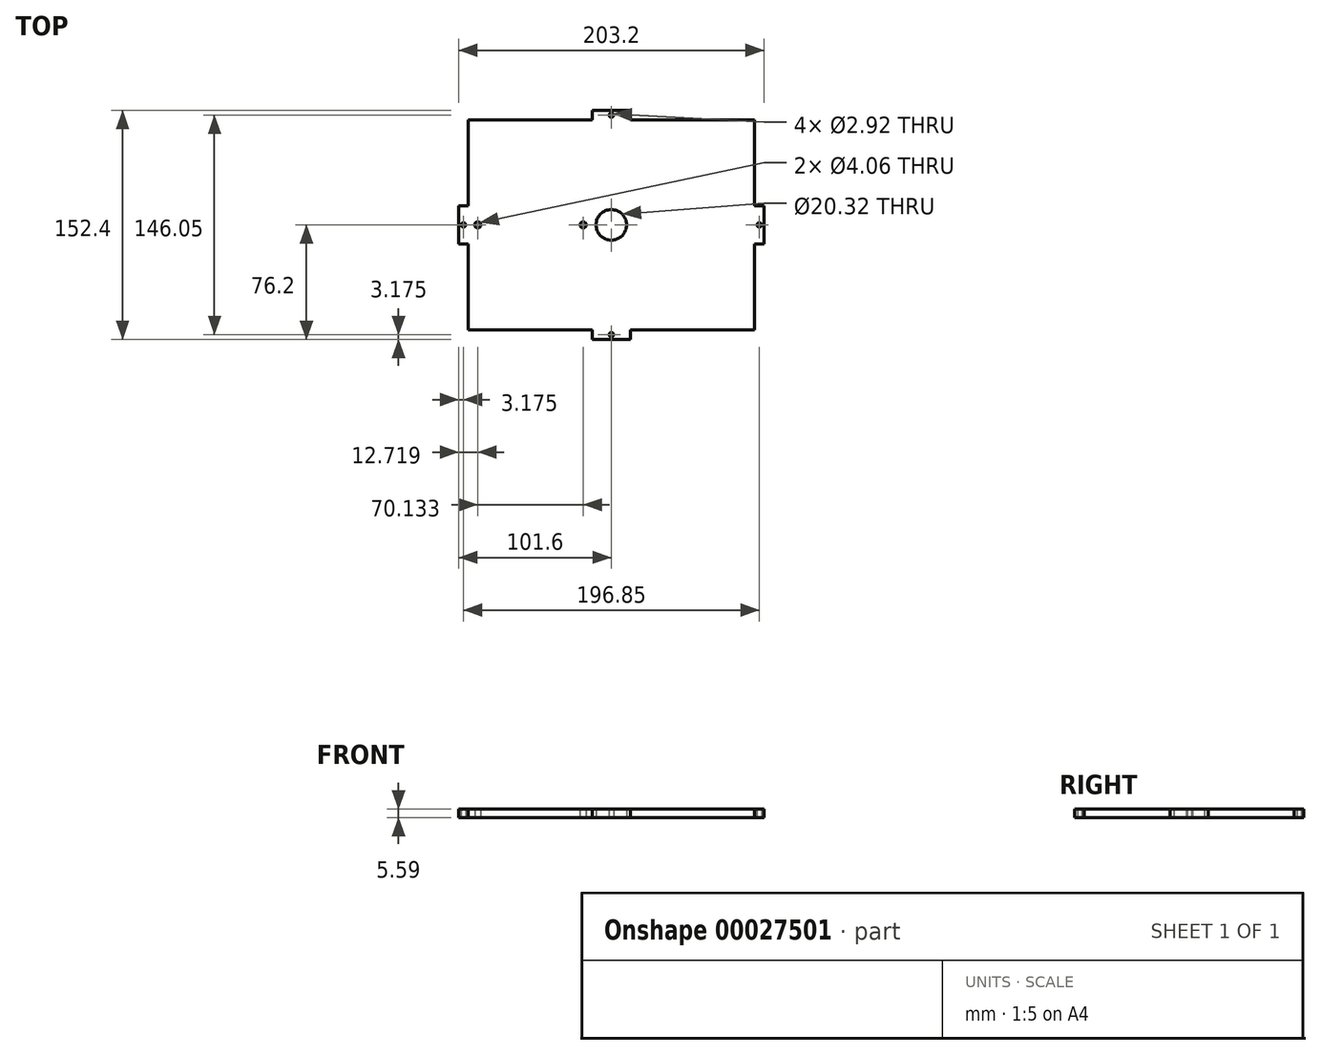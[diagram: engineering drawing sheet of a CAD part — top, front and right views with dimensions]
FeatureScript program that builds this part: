
annotation { "Feature Type Name" : "Feature", "Feature Type Description" : "" }
export const myFeature = defineFeature(function(context is Context, id is Id, definition is map)
    precondition{}
    {
        {
            var Q0;
            Q0=qCreatedBy(makeId("Top.planeOp"),FACE);
            var sketch = newSketch(context, id + "F0", { "sketchPlane" : qUnion([Q0])});
            skLineSegment(sketch, "E0.rect.bottom", {"start": v(12.7, -76.2) * mm, "end": v(-12.7, -76.2) * mm});
            skLineSegment(sketch, "E0.rect.top", {"start": v(12.7, 76.2) * mm, "end": v(-12.7, 76.2) * mm});
            skLineSegment(sketch, "E0.rect.left", {"start": v(101.6, -12.7) * mm, "end": v(101.6, 12.7) * mm});
            skLineSegment(sketch, "E0.rect.right", {"start": v(-101.6, -12.7) * mm, "end": v(-101.6, 12.7) * mm});
            skPoint(sketch, "E0.rect.middle", {"position": v(0, 0) * mm});
            skLineSegment(sketch, "E1", {"start": v(0, 76.2) * mm, "end": v(0, 69.85) * mm, "construction": true});
            skLineSegment(sketch, "E2", {"start": v(0, 0) * mm, "end": v(101.6, 0) * mm, "construction": true});
            skPoint(sketch, "E3.orphan", {"position": v(-101.6, 0) * mm});
            skLineSegment(sketch, "E4", {"start": v(0, 0) * mm, "end": v(-95.25, 0) * mm, "construction": true});
            skLineSegment(sketch, "E5", {"start": v(0, 0) * mm, "end": v(0, -76.2) * mm, "construction": true});
            skPoint(sketch, "E6.rect.middle", {"position": v(-50.8, 0) * mm});
            skCircle(sketch, "E7", {"center": v(0, 0) * mm, "radius": 10.16 * mm});
            skLineSegment(sketch, "E8.0", {"start": v(95.25, 69.85) * mm, "end": v(12.7, 69.85) * mm});
            skLineSegment(sketch, "E8.1", {"start": v(95.25, -69.85) * mm, "end": v(95.25, -12.7) * mm});
            skLineSegment(sketch, "E8.2", {"start": v(95.25, -69.85) * mm, "end": v(12.7, -69.85) * mm});
            skLineSegment(sketch, "E8.3", {"start": v(-95.25, -69.85) * mm, "end": v(-95.25, -12.7) * mm});
            skLineSegment(sketch, "E9.0", {"start": v(0, 12.7) * mm, "end": v(-16.5, 12.7) * mm, "construction": true});
            skLineSegment(sketch, "E10.0", {"start": v(0, -12.7) * mm, "end": v(-101.6, -12.7) * mm, "construction": true});
            skLineSegment(sketch, "E11", {"start": v(-101.6, 12.7) * mm, "end": v(-95.25, 12.7) * mm});
            skLineSegment(sketch, "E12", {"start": v(-95.25, -12.7) * mm, "end": v(-101.6, -12.7) * mm});
            skPoint(sketch, "E13.orphan", {"position": v(-101.6, -76.2) * mm});
            skPoint(sketch, "E14.orphan", {"position": v(-101.6, 76.2) * mm});
            skLineSegment(sketch, "E15.0", {"start": v(-12.7, 0) * mm, "end": v(-12.7, -76.2) * mm, "construction": true});
            skLineSegment(sketch, "E16.0", {"start": v(12.7, 0) * mm, "end": v(12.7, -76.2) * mm, "construction": true});
            skLineSegment(sketch, "E17", {"start": v(-12.7, -69.85) * mm, "end": v(-12.7, -76.2) * mm});
            skLineSegment(sketch, "E18", {"start": v(12.7, -69.85) * mm, "end": v(12.7, -76.2) * mm});
            skPoint(sketch, "E19.orphan", {"position": v(101.6, -76.2) * mm});
            skLineSegment(sketch, "E20.MirrorCS", {"start": v(101.6, 12.7) * mm, "end": v(95.25, 12.7) * mm});
            skLineSegment(sketch, "E21.MirrorCS", {"start": v(95.25, -12.7) * mm, "end": v(101.6, -12.7) * mm});
            skLineSegment(sketch, "E22.MirrorCS", {"start": v(12.7, 69.85) * mm, "end": v(12.7, 76.2) * mm});
            skLineSegment(sketch, "E23.MirrorCS", {"start": v(-12.7, 69.85) * mm, "end": v(-12.7, 76.2) * mm});
            skPoint(sketch, "E24.orphan", {"position": v(101.6, 76.2) * mm});
            skLineSegment(sketch, "E25.trimOffspring", {"start": v(-12.7, -69.85) * mm, "end": v(-95.25, -69.85) * mm});
            skLineSegment(sketch, "E26.trimOffspring", {"start": v(-95.25, 12.7) * mm, "end": v(-95.25, 69.85) * mm});
            skLineSegment(sketch, "E27.trimOffspring", {"start": v(-12.7, 69.85) * mm, "end": v(-95.25, 69.85) * mm});
            skLineSegment(sketch, "E28.trimOffspring", {"start": v(95.25, 12.7) * mm, "end": v(95.25, 69.85) * mm});
            skLineSegment(sketch, "E29", {"start": v(-95.25, 12.7) * mm, "end": v(-95.25, 0) * mm, "construction": true});
            skLineSegment(sketch, "E30", {"start": v(-12.7, 69.85) * mm, "end": v(0, 69.85) * mm, "construction": true});
            skLineSegment(sketch, "E31", {"start": v(-95.25, 0) * mm, "end": v(-95.25, -12.7) * mm, "construction": true});
            skLineSegment(sketch, "E32", {"start": v(-95.25, 0) * mm, "end": v(-101.6, 0) * mm, "construction": true});
            skLineSegment(sketch, "E33", {"start": v(0, 69.85) * mm, "end": v(12.7, 69.85) * mm, "construction": true});
            skLineSegment(sketch, "E34", {"start": v(0, 69.85) * mm, "end": v(0, 0) * mm, "construction": true});
            skCircle(sketch, "E35", {"center": v(0, 73.02) * mm, "radius": 1.46 * mm});
            skCircle(sketch, "E36", {"center": v(-98.42, 0) * mm, "radius": 1.46 * mm});
            skCircle(sketch, "E37.MirrorC", {"center": v(0, -73.02) * mm, "radius": 1.46 * mm});
            skCircle(sketch, "E38.MirrorC", {"center": v(98.42, 0) * mm, "radius": 1.46 * mm});
            skLineSegment(sketch, "E39", {"start": v(-82.55, 12.7) * mm, "end": v(-82.55, -12.7) * mm, "construction": true});
            skLineSegment(sketch, "E40", {"start": v(-16.5, 12.7) * mm, "end": v(-16.5, -12.7) * mm, "construction": true});
            skLineSegment(sketch, "E41", {"start": v(-90.97, 12.7) * mm, "end": v(-90.97, -12.7) * mm, "construction": true});
            skLineSegment(sketch, "E42", {"start": v(-12.23, 12.7) * mm, "end": v(-12.23, -12.7) * mm, "construction": true});
            skCircle(sketch, "E43", {"center": v(-88.88, 0) * mm, "radius": 2.03 * mm});
            skLineSegment(sketch, "E44", {"start": v(-82.55, 12.7) * mm, "end": v(-101.6, 12.7) * mm, "construction": true});
            skLineSegment(sketch, "E45", {"start": v(-16.5, 12.7) * mm, "end": v(-82.55, 12.7) * mm, "construction": true});
            skLineSegment(sketch, "E46", {"start": v(-49.53, 12.7) * mm, "end": v(-49.53, -12.7) * mm, "construction": true});
            skLineSegment(sketch, "E47", {"start": v(-86.85, 0) * mm, "end": v(-86.85, -12.7) * mm, "construction": true});
            skLineSegment(sketch, "E48", {"start": v(-86.85, 0) * mm, "end": v(-86.85, 22.57) * mm, "construction": true});
            skLineSegment(sketch, "E49", {"start": v(-86.85, 22.57) * mm, "end": v(-20.8, 22.57) * mm, "construction": true});
            skLineSegment(sketch, "E50", {"start": v(-20.8, 22.57) * mm, "end": v(-20.8, -12.7) * mm, "construction": true});
            skCircle(sketch, "E51", {"center": v(-18.75, 0) * mm, "radius": 2.03 * mm});
            skSolve(sketch);
        }
        {
            var Q0;
            Q0=makeQuery(id+"F0.imprint","IMPRINT",FACE,{"disambiguationData":[TD([[makeQuery(id+"F0.imprint","IMPRINT",EDGE,{"derivedFrom":sQuery(id+"F0.wireOp",EDGE,"E0.rect.bottom")}),-1.0]])]});
            extrude(context, id + "F1", {"entities" : qUnion([Q0]), "depth" : 5.6 * mm});
        }
    });
